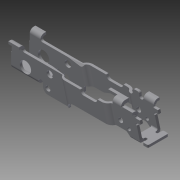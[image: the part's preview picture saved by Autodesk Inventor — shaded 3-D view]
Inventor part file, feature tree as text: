
AUTODESK INVENTOR PART (.ipt)
format: ipt  version: 2014 SP2 (Build 180246200, 246)  size: 4,402,176 bytes
history: native  units: in
note: dims shown in document units (in); Inventor stores cm internally (conversion verified against a paired STEP export)
features: projected_geometry x29, sketch x27, extrude x19, fillet x12, other x4, mirror x4, plane x4, sweep x3, revolve x1, loft x1
ambient origin geometry x8: Origin, YZ Plane, XZ Plane, XY Plane, X Axis, Y Axis, Z Axis, Center Point
bodies: Solid1 (feature_tree)
feature tree (104):
  other  "Frame"
  extrude  "Extrusion1"  Depth=0.3565in
  extrude  "Extrusion2"  Depth=0.157in
  extrude  "Extrusion3"  Depth=0.242in
  mirror  "Mirror1"
  extrude  "Extrusion4"  Depth=0.152in
  extrude  "Extrusion5"  Depth=0.2745in
  extrude  "Extrusion6"  Depth=0.338in
  mirror  "Mirror2"
  fillet  "Fillet1"  Radius=0.8175in
  sweep  "Sweep1"
  sketch  "Sketch8"  dims[d46=0.468in d52=0.7795in]
  sweep  "Sweep2"
  sweep  "Sweep3"
  mirror  "Mirror3"
  fillet  "Fillet2"  Radius=0.0938in
  fillet  "Fillet3"  Radius=0.113in
  fillet  "Fillet4"  Radius=0.092in
  fillet  "Fillet5"  Radius=0.781in
  extrude  "Extrusion7"  Depth=3.916in
  fillet  "Fillet6"  Radius=0.328in
  extrude  "Extrusion8"  TaperAngle=75.0deg  [1 undecoded]
  extrude  "Extrusion9"  Depth=0.0375in
  fillet  "Fillet7"  Radius=0.2in
  extrude  "Extrusion10"  Depth=0.1365in
  extrude  "Extrusion11"  Depth=0.125in
  fillet  "Fillet8"  Radius=0.125in
  extrude  "Extrusion12"  Depth=0.896in TaperAngle=0.0deg
  extrude  "Extrusion13"  Depth=0.077in
  extrude  "Extrusion14"  Depth=0.077in
  fillet  "Fillet9"  Radius=0.077in
  extrude  "Extrusion15"  Depth=0.2035in
  extrude  "Extrusion16"  Depth=0.1245in TaperAngle=0.0deg
  extrude  "Extrusion17"  Depth=0.077in
  fillet  "Fillet10"  Radius=0.1245in
  fillet  "Fillet11"  Radius=0.125in
  revolve  "Revolution1"  [1 undecoded]
  extrude  "Extrusion18"  Depth=0.125in
  fillet  "Fillet12"  Radius=0.048in
  plane  "Work Plane1"
  sketch  "Sketch23"  dims[d195=0.0in d196=0.125in d198=0.048in]
  plane  "Work Plane2"
  loft  "Loft1"
  mirror  "Mirror4"
  plane  "Work Plane3"
  plane  "Work Plane4"
  extrude  "Extrusion19"  Depth=0.856in
  sketch  "Sketch1"  dims[d1=4.685in d7=0.3565in]
  other  "Image1"
  sketch  "Sketch2"  dims[d10=0.2in d11=0.157in]
  projected_geometry  "Projected Loop1"
  projected_geometry  "Projected Loop2"
  sketch  "Sketch3"  dims[d12=0.514in d13=0.242in]
  projected_geometry  "Projected Loop3"
  sketch  "Sketch4"  dims[d14=0.487in d15=0.152in]
  sketch  "Sketch5"  dims[d27=0.2035in d29=0.2745in]
  projected_geometry  "Projected Loop4"
  sketch  "Sketch6"  dims[d32=0.6545in d33=0.017in d34=0.338in d35=0.8175in]
  projected_geometry  "Projected Loop5"
  sketch  "Sketch7"  dims[d37=0.0625in d41=0.855in]
  projected_geometry  "Projected Loop6"
  sketch  "3D Sketch1"
  projected_geometry  "Projected Loop7"
  sketch  "3D Sketch2"
  sketch  "3D Sketch3"
  sketch  "Sketch10"  dims[d61=0.076in d63=0.0905in d78=0.0938in d96=0.113in d100=0.092in d103=0.781in]
  projected_geometry  "Projected Loop9"
  sketch  "Sketch11"  dims[d107=0.0875in d109=3.916in d110=0.328in]
  projected_geometry  "Projected Loop10"
  sketch  "Sketch12"  dims[d114=0.067in d119=75.0deg]
  projected_geometry  "Projected Loop11"
  sketch  "Sketch13"  dims[d129=0.0375in d146=0.5275in d151=0.2in]
  projected_geometry  "Projected Loop12"
  sketch  "Sketch14"  dims[d152=0.108in d153=0.1365in]
  projected_geometry  "Projected Loop13"
  sketch  "Sketch15"  dims[d157=0.078in d158=0.6225in d165=0.125in]
  other  "Image2"
  projected_geometry  "Projected Loop14"
  projected_geometry  "Projected Loop15"
  projected_geometry  "Projected Loop16"
  projected_geometry  "Projected Loop17"
  projected_geometry  "Projected Loop18"
  projected_geometry  "Projected Loop19"
  sketch  "Sketch16"  dims[d168=0.258in d173=0.896in d174=0.0in]
  projected_geometry  "Projected Loop20"
  sketch  "Sketch17"  dims[d175=0.493in d176=0.077in]
  projected_geometry  "Projected Loop21"
  sketch  "Sketch18"  dims[d177=0.896in d178=0.0in d179=0.73in d180=0.077in]
  projected_geometry  "Projected Loop22"
  sketch  "Sketch19"  dims[d181=0.1245in d182=0.0in d183=0.2035in]
  projected_geometry  "Projected Loop23"
  sketch  "Sketch20"  dims[d184=0.1245in d185=0.0in d186=0.1245in d187=0.0in]
  projected_geometry  "Projected Loop24"
  sketch  "Sketch21"  dims[d188=0.077in d189=0.077in d190=0.1245in d191=0.0in d192=0.125in]
  projected_geometry  "Projected Loop25"
  sketch  "Sketch22"  dims[d193=0.0in d194=0.0in]
  projected_geometry  "Projected Loop26"
  other  "Work Axis1"
  sketch  "Sketch24"  dims[d199=0.048in d200=0.125in]
  sketch  "Sketch25"  dims[d201=0.2865in d202=0.088in d203=0.1245in d204=0.0in d205=0.048in d206=0.336in d207=0.0565in d208=0.0in d209=0.103in d210=0.338in d211=0.0565in d212=0.0in d213=0.0362in d215=0.111in d216=0.0565in d217=0.0in d218=0.0565in d219=0.0in d220=0.01in d222=4.64in d233=0.3045in d235=0.0855in d237=0.06in d238=0.177in d241=0.5405in d242=0.0in d243=0.27in d244=0.0in d245=0.5405in d246=0.0in d252=0.5405in d253=0.0in d254=0.0625in d255=0.078in d257=0.564in d258=0.245in d259=0.0in d260=0.245in d261=0.0in d262=0.09in d263=0.245in d264=0.0in d265=0.125in d266=0.048in d267=0.1718in d268=0.05in d269=0.05in d270=0.2675in d271=0.086in d272=0.0115in d273=0.0in d274=0.0115in d275=0.0in d276=0.533in d277=0.0in d278=90.0deg d279=0.0in d280=90.0deg d281=0.856in d282=1.0in d283=0.0in d284=0.172in]
  projected_geometry  "Projected Loop27"
  projected_geometry  "Projected Loop28"
  projected_geometry  "Project Cut Edges1"
  projected_geometry  "Project Cut Edges2"
note: 2 required parameter values undecoded (feature->parameter linkage not recoverable at this tier; creation-order binding heuristic only, values carry confidence <= 0.55)